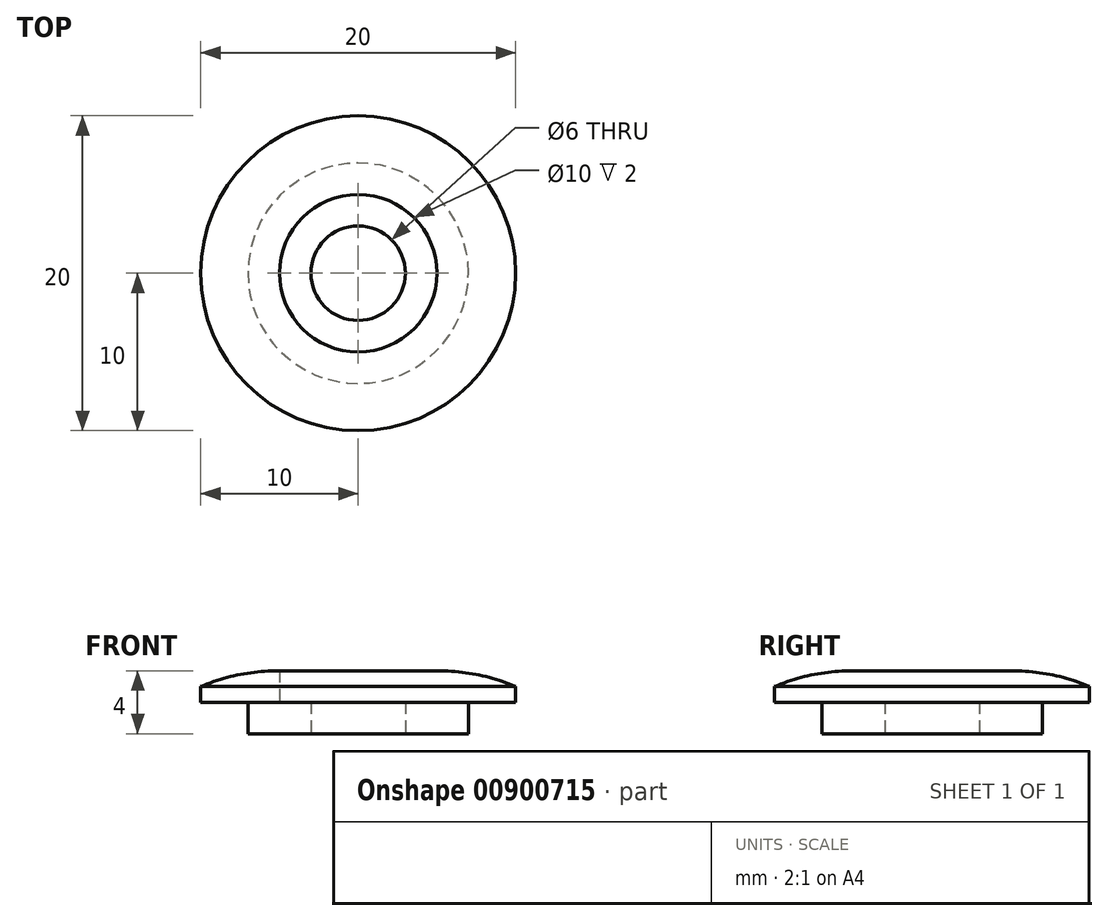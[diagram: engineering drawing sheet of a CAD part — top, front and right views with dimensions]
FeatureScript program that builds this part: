
annotation { "Feature Type Name" : "Feature", "Feature Type Description" : "" }
export const myFeature = defineFeature(function(context is Context, id is Id, definition is map)
    precondition{}
    {
        {
            var Q0;
            Q0=qCreatedBy(makeId("Front.planeOp"),FACE);
            var sketch = newSketch(context, id + "F0", { "sketchPlane" : qUnion([Q0])});
            skLineSegment(sketch, "E0", {"start": v(0, 0) * mm, "end": v(-4, 0) * mm});
            skLineSegment(sketch, "E1", {"start": v(-4, 0) * mm, "end": v(-4, 2) * mm});
            skLineSegment(sketch, "E2", {"start": v(-4, 2) * mm, "end": v(-7, 2) * mm});
            skLineSegment(sketch, "E3", {"start": v(-7, 2) * mm, "end": v(-7, 3) * mm});
            skArc(sketch, "E4", {"start": v(-2, 4) * mm, "mid": v(-4.55, 3.75) * mm, "end": v(-7, 3) * mm});
            skLineSegment(sketch, "E5", {"start": v(0, 2) * mm, "end": v(0, 2) * mm});
            skLineSegment(sketch, "E6", {"start": v(-2, 2) * mm, "end": v(-2, 4) * mm});
            skLineSegment(sketch, "E7", {"start": v(0, 2) * mm, "end": v(-2, 2) * mm});
            skLineSegment(sketch, "E8", {"start": v(3, 0) * mm, "end": v(3, 2) * mm, "construction": true});
            skLineSegment(sketch, "E9", {"start": v(0, 2) * mm, "end": v(0, 0) * mm});
            skLineSegment(sketch, "E10", {"start": v(0, 0) * mm, "end": v(3, 0) * mm});
            skLineSegment(sketch, "E11", {"start": v(0, 2) * mm, "end": v(3, 2) * mm});
            skSolve(sketch);
        }
        {
            var Q0;
            Q0 = qSketchRegion(id + "F0", true);
            var Q1;
            Q1=sQuery(id+"F0.wireOp",EDGE,"E8");
            revolve(context, id + "F1", {"surfaceOperationType" : NewSurfaceOperationType.NEW, "entities" : qUnion([Q0]), "axis" : qUnion([Q1]), "revolveType" : RevolveType.FULL});
        }
    });
